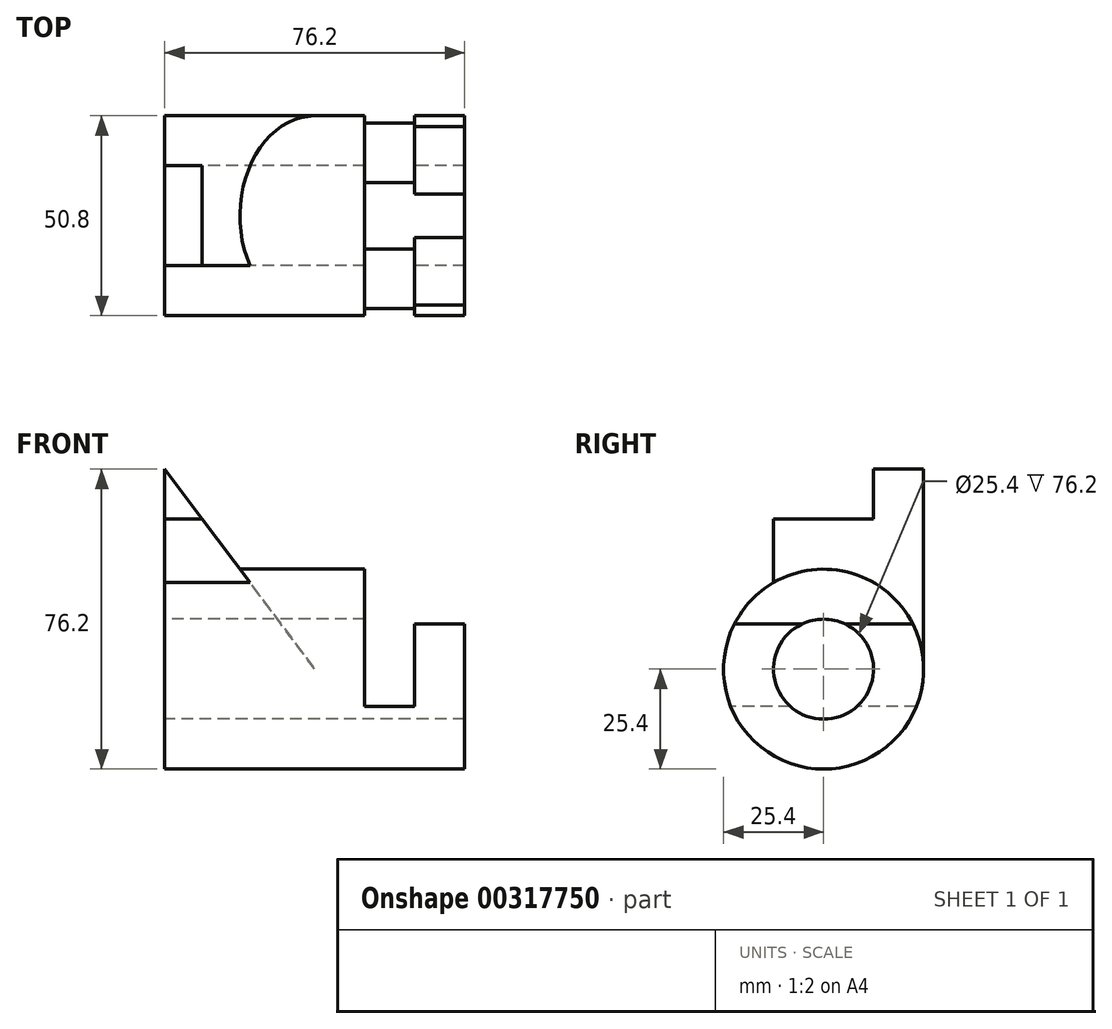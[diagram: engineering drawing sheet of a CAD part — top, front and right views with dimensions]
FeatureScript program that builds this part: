
annotation { "Feature Type Name" : "Feature", "Feature Type Description" : "" }
export const myFeature = defineFeature(function(context is Context, id is Id, definition is map)
    precondition{}
    {
        {
            var Q0;
            Q0=qCreatedBy(makeId("Right.planeOp"),FACE);
            var sketch = newSketch(context, id + "F0", { "sketchPlane" : qUnion([Q0])});
            skCircle(sketch, "E0", {"center": v(0, 0) * mm, "radius": 12.7 * mm});
            skCircle(sketch, "E1", {"center": v(0, 0) * mm, "radius": 25.4 * mm});
            skSolve(sketch);
        }
        {
            var Q0;
            Q0=makeQuery(id+"F0.imprint","IMPRINT",FACE,{"disambiguationData":[TD([[makeQuery(id+"F0.imprint","IMPRINT",EDGE,{"derivedFrom":sQuery(id+"F0.wireOp",EDGE,"E0")}),-1.0]])]});
            extrude(context, id + "F1", {"entities" : qUnion([Q0]), "depth" : 50.8 * mm});
        }
        {
            var Q0;
            Q0=qCreatedBy(makeId("Right.planeOp"),FACE);
            var sketch = newSketch(context, id + "F2", { "sketchPlane" : qUnion([Q0])});
            skLineSegment(sketch, "E2", {"start": v(-12.7, 0) * mm, "end": v(-12.7, 38.1) * mm});
            skLineSegment(sketch, "E3", {"start": v(-12.7, 38.1) * mm, "end": v(12.7, 38.1) * mm});
            skLineSegment(sketch, "E4", {"start": v(12.7, 38.1) * mm, "end": v(12.7, 50.8) * mm});
            skLineSegment(sketch, "E5", {"start": v(12.7, 50.8) * mm, "end": v(25.4, 50.8) * mm});
            skLineSegment(sketch, "E6", {"start": v(25.4, 50.8) * mm, "end": v(25.4, 0) * mm});
            skLineSegment(sketch, "E7", {"start": v(25.4, 0) * mm, "end": v(-12.7, 0) * mm});
            skSolve(sketch);
        }
        {
            var Q0;
            Q0=makeQuery(id+"F2.imprint","IMPRINT",FACE,{"disambiguationData":[TD([[makeQuery(id+"F2.imprint","IMPRINT",EDGE,{"derivedFrom":sQuery(id+"F2.wireOp",EDGE,"E2")}),-1.0]])]});
            extrude(context, id + "F3", {"entities" : qUnion([Q0]), "operationType" : NewBodyOperationType.ADD, "depth" : 38.1 * mm});
        }
        {
            var Q0;
            Q0=makeQuery(id+"F3.opExtrude","SWEPT_FACE",FACE,{"disambiguationData":[OSD([sQuery(id+"F2.wireOp",EDGE,"E6")])]});
            var sketch = newSketch(context, id + "F4", { "sketchPlane" : qUnion([Q0])});
            skLineSegment(sketch, "E8", {"start": v(0, 50.8) * mm, "end": v(-38.1, 0) * mm});
            skLineSegment(sketch, "E9", {"start": v(-38.1, 0) * mm, "end": v(0, 0) * mm});
            skLineSegment(sketch, "E10", {"start": v(0, 0) * mm, "end": v(0, 50.8) * mm});
            skLineSegment(sketch, "E11", {"start": v(0, 50.8) * mm, "end": v(-38.1, 50.8) * mm});
            skLineSegment(sketch, "E12", {"start": v(-38.1, 50.8) * mm, "end": v(-38.1, 0) * mm});
            skSolve(sketch);
        }
        {
            var Q0;
            Q0=makeQuery(id+"F4.imprint","IMPRINT",FACE,{"disambiguationData":[TD([[makeQuery(id+"F4.imprint","IMPRINT",EDGE,{"derivedFrom":sQuery(id+"F4.wireOp",EDGE,"E8")}),-1.0]])]});
            extrude(context, id + "F5", {"entities" : qUnion([Q0]), "operationType" : NewBodyOperationType.REMOVE, "endBound" : BoundingType.THROUGH_ALL, "oppositeDirection" : true, "depth" : 25.4 * mm});
        }
        {
            var Q0;
            Q0=makeQuery(id+"F5.boolean.opBoolean","COPY",FACE,{"derivedFrom":makeQuery(id+"F5.opExtrude","SWEPT_FACE",FACE,{"disambiguationData":[OSD([sQuery(id+"F4.wireOp",EDGE,"E12")])]})});
            extrude(context, id + "F6", {"entities" : qUnion([Q0]), "operationType" : NewBodyOperationType.ADD, "depth" : 25.4 * mm});
        }
        {
            var Q0;
            Q0=makeQuery(id+"F0.imprint","IMPRINT",FACE,{"disambiguationData":[TD([[makeQuery(id+"F0.imprint","IMPRINT",EDGE,{"derivedFrom":sQuery(id+"F0.wireOp",EDGE,"E0")}),1.0]])]});
            extrude(context, id + "F7", {"entities" : qUnion([Q0]), "operationType" : NewBodyOperationType.REMOVE, "endBound" : BoundingType.THROUGH_ALL, "depth" : 25.4 * mm});
        }
        {
            var Q0;
            Q0=makeQuery(id+"F1.opExtrude","CAP_FACE",FACE,{"disambiguationData":[OSD([sQuery(id+"F0.wireOp",EDGE,"E0"),sQuery(id+"F0.wireOp",EDGE,"E1")])],"isStart":false});
            var sketch = newSketch(context, id + "F8", { "sketchPlane" : qUnion([Q0])});
            skLineSegment(sketch, "E13", {"start": v(-22.68, 11.43) * mm, "end": v(22.68, 11.43) * mm});
            skArc(sketch, "E14", {"start": v(-22.68, 11.43) * mm, "mid": v(0, -25.4) * mm, "end": v(22.68, 11.43) * mm});
            skSolve(sketch);
        }
        {
            var Q0;
            {var subQ0=sQuery(id+"F8.wireOp",EDGE,"ooKVRRT4-YYT5-GblT-T90O-fPDKf1AoL7D5");Q0=makeQuery(id+"F8.imprint","IMPRINT",FACE,{"disambiguationData":[TD([[makeQuery(id+"F8.imprint","IMPRINT",EDGE,{"derivedFrom":subQ0}),1.0]])]});}
            var Q1;
            {var subQ0=sQuery(id+"F8.wireOp",EDGE,"E14");Q1=makeQuery(id+"F8.imprint","IMPRINT",FACE,{"disambiguationData":[TD([[makeQuery(id+"F8.imprint","IMPRINT",EDGE,{"derivedFrom":subQ0}),1.0]])]});}
            extrude(context, id + "F9", {"entities" : qUnion([Q0, Q1]), "operationType" : NewBodyOperationType.ADD, "depth" : 25.4 * mm});
        }
        {
            var Q0;
            Q0=qCreatedBy(makeId("Front.planeOp"),FACE);
            var sketch = newSketch(context, id + "F10", { "sketchPlane" : qUnion([Q0])});
            skLineSegment(sketch, "E15.bottom", {"start": v(50.8, 25.4) * mm, "end": v(63.5, 25.4) * mm});
            skLineSegment(sketch, "E15.top", {"start": v(50.8, -9.53) * mm, "end": v(63.5, -9.53) * mm});
            skLineSegment(sketch, "E15.left", {"start": v(50.8, 25.4) * mm, "end": v(50.8, -9.53) * mm});
            skLineSegment(sketch, "E15.right", {"start": v(63.5, 25.4) * mm, "end": v(63.5, -9.53) * mm});
            skSolve(sketch);
        }
        {
            var Q0;
            Q0=makeQuery(id+"F10.imprint","IMPRINT",FACE,{"disambiguationData":[TD([[makeQuery(id+"F10.imprint","IMPRINT",EDGE,{"derivedFrom":sQuery(id+"F10.wireOp",EDGE,"E15.bottom")}),-1.0]])]});
            extrude(context, id + "F11", {"entities" : qUnion([Q0]), "operationType" : NewBodyOperationType.REMOVE, "endBound" : BoundingType.THROUGH_ALL, "oppositeDirection" : true, "depth" : 25.4 * mm, "hasSecondDirection" : true, "secondDirectionOppositeDirection" : false, "secondDirectionDepth" : 25.4 * mm});
        }
    });
